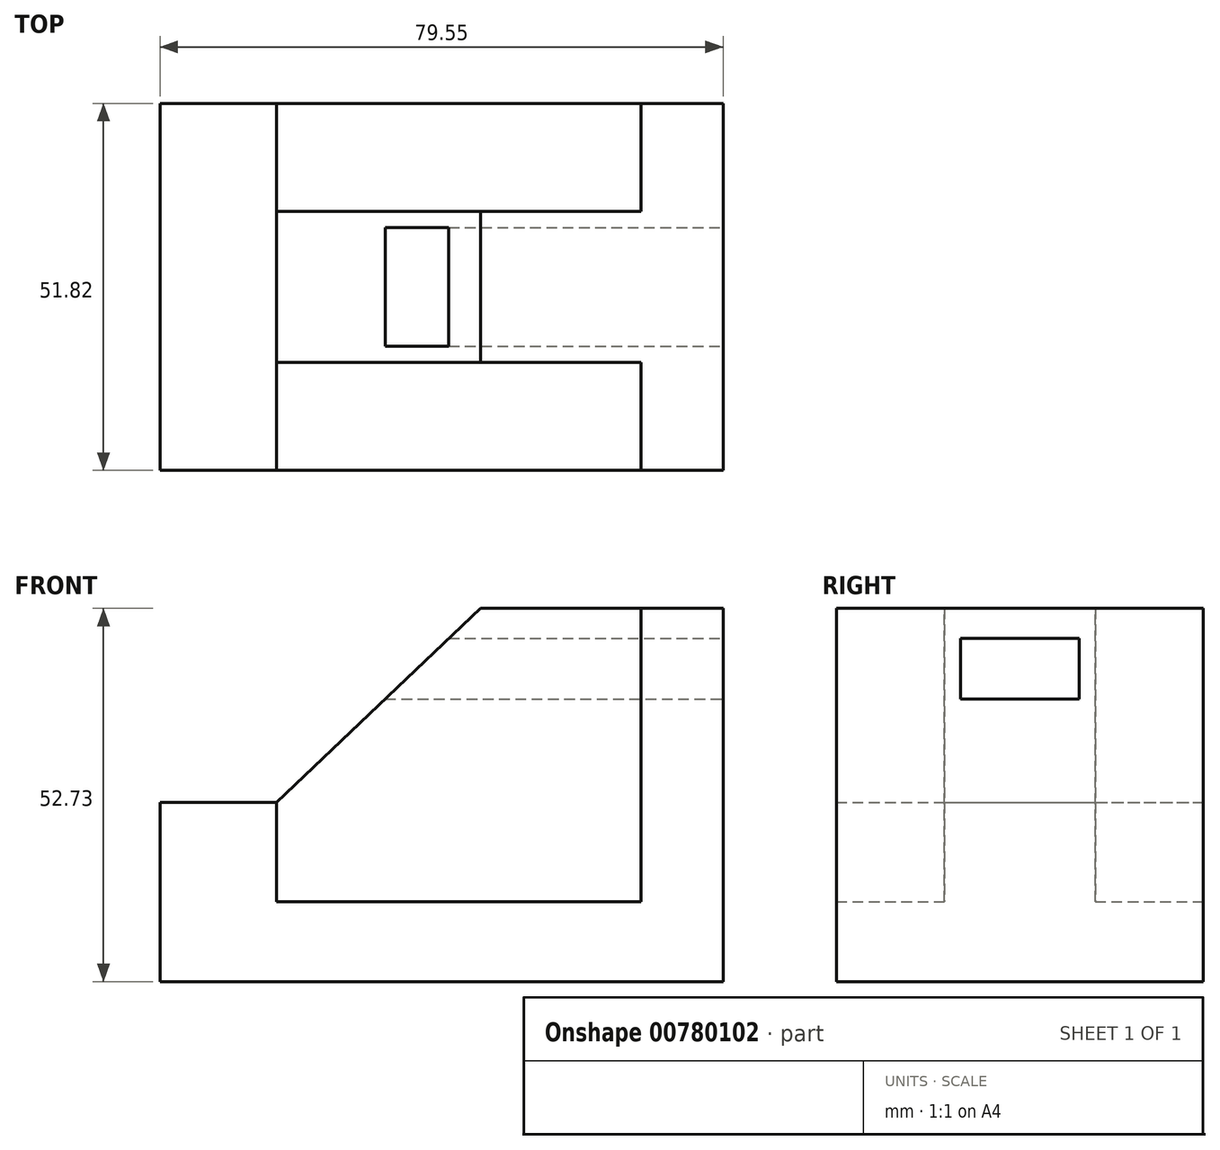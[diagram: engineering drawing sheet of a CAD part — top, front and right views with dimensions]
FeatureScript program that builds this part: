
annotation { "Feature Type Name" : "Feature", "Feature Type Description" : "" }
export const myFeature = defineFeature(function(context is Context, id is Id, definition is map)
    precondition{}
    {
        {
            var Q0;
            Q0=qCreatedBy(makeId("Front.planeOp"),FACE);
            var sketch = newSketch(context, id + "F0", { "sketchPlane" : qUnion([Q0])});
            skLineSegment(sketch, "E0", {"start": v(34.3, 0) * mm, "end": v(0, 0) * mm});
            skLineSegment(sketch, "E1", {"start": v(0, 0) * mm, "end": v(-28.8, -27.43) * mm});
            skLineSegment(sketch, "E2", {"start": v(-28.8, -27.43) * mm, "end": v(-45.26, -27.43) * mm});
            skLineSegment(sketch, "E3", {"start": v(-45.26, -27.43) * mm, "end": v(-45.26, -52.73) * mm});
            skLineSegment(sketch, "E4", {"start": v(-45.26, -52.73) * mm, "end": v(34.3, -52.73) * mm});
            skLineSegment(sketch, "E5", {"start": v(34.3, 0) * mm, "end": v(34.3, -52.73) * mm});
            skLineSegment(sketch, "E6", {"start": v(-28.8, -27.43) * mm, "end": v(-28.8, -41.45) * mm});
            skLineSegment(sketch, "E7", {"start": v(-28.8, -41.45) * mm, "end": v(22.7, -41.45) * mm});
            skLineSegment(sketch, "E8", {"start": v(22.7, -41.45) * mm, "end": v(22.7, 0) * mm});
            skSolve(sketch);
        }
        {
            var Q0;
            Q0=makeQuery(id+"F0.imprint","IMPRINT",FACE,{"disambiguationData":[TD([[makeQuery(id+"F0.imprint","IMPRINT",EDGE,{"derivedFrom":sQuery(id+"F0.wireOp",EDGE,"E2")}),1.0]])]});
            extrude(context, id + "F1", {"entities" : qUnion([Q0]), "endBound" : BoundingType.SYMMETRIC, "depth" : 51.82 * mm, "offsetDistance" : 25.4 * mm});
        }
        {
            var Q0;
            {var subQ0=sQuery(id+"F0.wireOp",EDGE,"E1");Q0=makeQuery(id+"F0.imprint","IMPRINT",FACE,{"disambiguationData":[TD([[makeQuery(id+"F0.imprint","IMPRINT",EDGE,{"derivedFrom":subQ0}),1.0]])]});}
            extrude(context, id + "F2", {"entities" : qUnion([Q0]), "operationType" : NewBodyOperationType.ADD, "endBound" : BoundingType.SYMMETRIC, "depth" : 21.34 * mm, "offsetDistance" : 25.4 * mm});
        }
        {
            var Q0;
            Q0=makeQuery(id+"F1.opExtrude","SWEPT_FACE",FACE,{"disambiguationData":[OSD([sQuery(id+"F0.wireOp",EDGE,"E5")])]});
            var sketch = newSketch(context, id + "F3", { "sketchPlane" : qUnion([Q0])});
            skLineSegment(sketch, "E9.bottom", {"start": v(8.38, -12.8) * mm, "end": v(-8.38, -12.8) * mm});
            skLineSegment(sketch, "E9.top", {"start": v(8.38, -4.26) * mm, "end": v(-8.38, -4.26) * mm});
            skLineSegment(sketch, "E9.left", {"start": v(8.38, -12.8) * mm, "end": v(8.38, -4.26) * mm});
            skLineSegment(sketch, "E9.right", {"start": v(-8.38, -12.8) * mm, "end": v(-8.38, -4.26) * mm});
            skPoint(sketch, "E9.middle", {"position": v(0, -8.53) * mm});
            skSolve(sketch);
        }
        {
            var Q0;
            Q0 = qSketchRegion(id + "F3", true);
            extrude(context, id + "F4", {"entities" : qUnion([Q0]), "operationType" : NewBodyOperationType.REMOVE, "oppositeDirection" : true, "depth" : 83.31 * mm, "offsetDistance" : 25.4 * mm});
        }
    });
